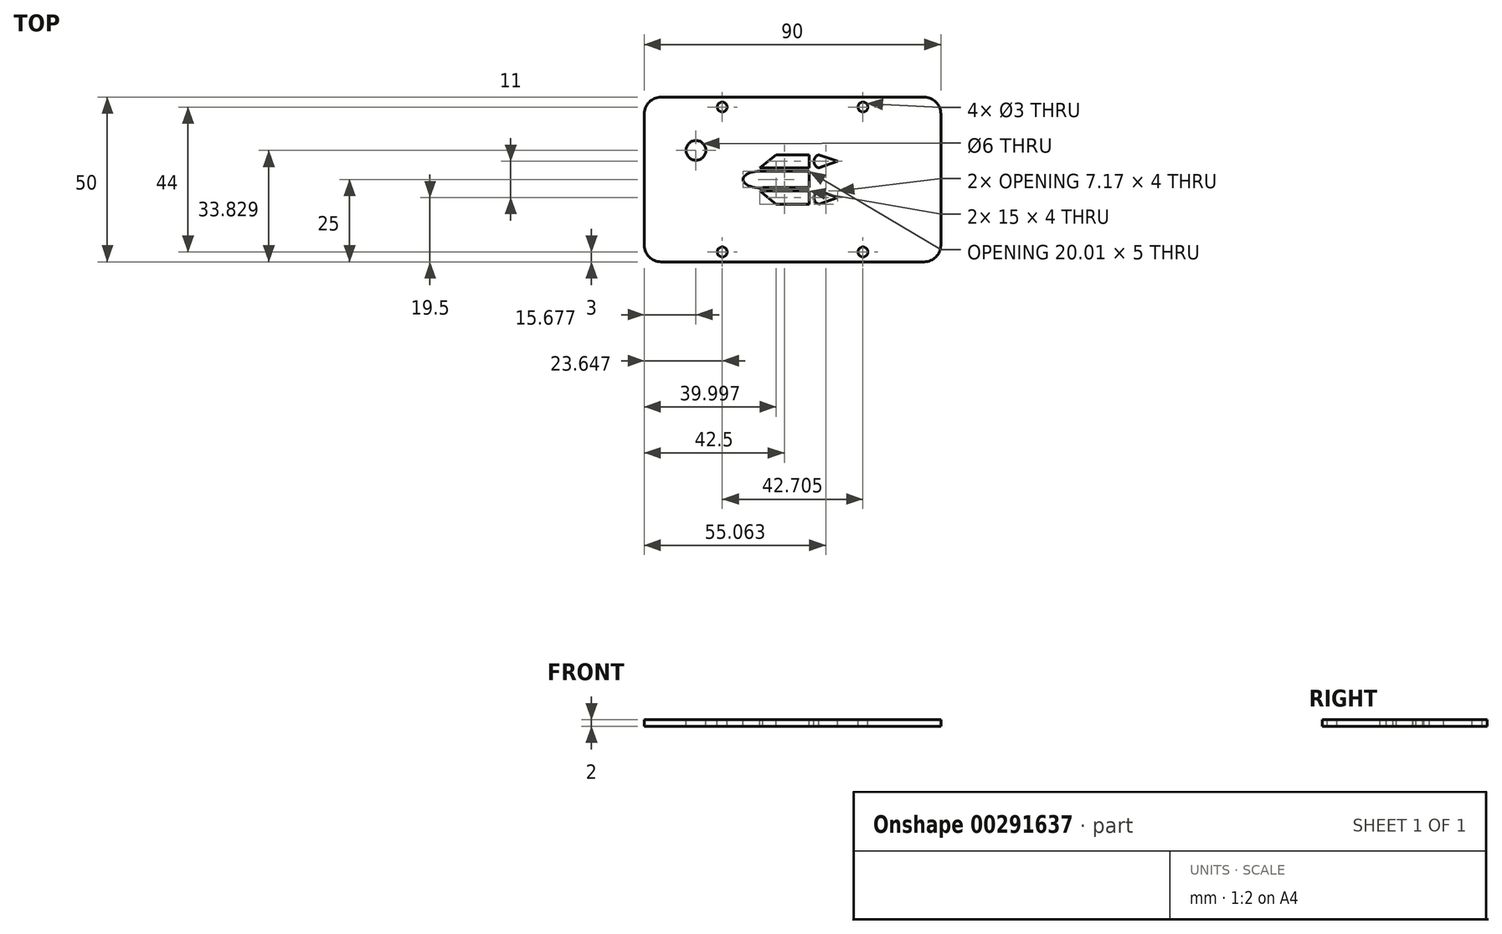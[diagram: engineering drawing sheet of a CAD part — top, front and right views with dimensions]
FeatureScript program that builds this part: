
annotation { "Feature Type Name" : "Feature", "Feature Type Description" : "" }
export const myFeature = defineFeature(function(context is Context, id is Id, definition is map)
    precondition{}
    {
        {
            var Q0;
            Q0=qCreatedBy(makeId("Top.planeOp"),FACE);
            var sketch = newSketch(context, id + "F0", { "sketchPlane" : qUnion([Q0])});
            skLineSegment(sketch, "E0.bottom", {"start": v(0, 0) * mm, "end": v(90, 0) * mm});
            skLineSegment(sketch, "E0.top", {"start": v(0, 50) * mm, "end": v(90, 50) * mm});
            skLineSegment(sketch, "E0.left", {"start": v(0, 0) * mm, "end": v(0, 50) * mm});
            skLineSegment(sketch, "E0.right", {"start": v(90, 0) * mm, "end": v(90, 50) * mm});
            skSolve(sketch);
        }
        {
            var Q0;
            Q0=qSketchRegion(id+"F0",true);
            extrude(context, id + "F1", {"entities" : qUnion([Q0]), "depth" : 2 * mm, "offsetDistance" : 25.4 * mm});
        }
        {
            var Q0;
            Q0=makeQuery(id+"F1.opExtrude","CAP_FACE",FACE,{"disambiguationData":[OSD([sQuery(id+"F0.wireOp",EDGE,"E0.bottom"),sQuery(id+"F0.wireOp",EDGE,"E0.top"),sQuery(id+"F0.wireOp",EDGE,"E0.left"),sQuery(id+"F0.wireOp",EDGE,"E0.right")])],"isStart":false});
            cPlane(context, id + "F2", {"entities" : qUnion([Q0]), "cplaneType" : CPlaneType.OFFSET, "offset" : 0 * mm, "width" : 152.4 * mm, "height" : 152.4 * mm});
        }
        {
            var Q0;
            Q0=makeQuery(id+"F1.opExtrude","SWEPT_EDGE",EDGE,{"disambiguationData":[OSD([sQuery(id+"F0.wireOp",EDGE,"E0.bottom"),sQuery(id+"F0.wireOp",EDGE,"E0.right")])]});
            fillet(context, id + "F3", {"entities" : qUnion([Q0]), "radius" : 5.08 * mm, "tangentPropagation" : true, "allowEdgeOverflow" : false});
        }
        {
            var Q0;
            Q0=makeQuery(id+"F1.opExtrude","SWEPT_EDGE",EDGE,{"disambiguationData":[OSD([sQuery(id+"F0.wireOp",EDGE,"E0.top"),sQuery(id+"F0.wireOp",EDGE,"E0.right")])]});
            fillet(context, id + "F4", {"entities" : qUnion([Q0]), "radius" : 5.08 * mm, "tangentPropagation" : true, "allowEdgeOverflow" : false});
        }
        {
            var Q0;
            Q0=makeQuery(id+"F1.opExtrude","SWEPT_EDGE",EDGE,{"disambiguationData":[OSD([sQuery(id+"F0.wireOp",EDGE,"E0.top"),sQuery(id+"F0.wireOp",EDGE,"E0.left")])]});
            fillet(context, id + "F5", {"entities" : qUnion([Q0]), "radius" : 5.08 * mm, "tangentPropagation" : true, "allowEdgeOverflow" : false});
        }
        {
            var Q0;
            Q0=makeQuery(id+"F1.opExtrude","SWEPT_EDGE",EDGE,{"disambiguationData":[OSD([sQuery(id+"F0.wireOp",EDGE,"E0.bottom"),sQuery(id+"F0.wireOp",EDGE,"E0.left")])]});
            fillet(context, id + "F6", {"entities" : qUnion([Q0]), "radius" : 5.08 * mm, "tangentPropagation" : true, "allowEdgeOverflow" : false});
        }
        {
            var Q0;
            Q0=qCreatedBy(id+"F2.planeOp",FACE);
            var sketch = newSketch(context, id + "F7", { "sketchPlane" : qUnion([Q0])});
            skLineSegment(sketch, "E1", {"start": v(45, 0) * mm, "end": v(45, 70.78) * mm});
            skLineSegment(sketch, "E2", {"start": v(0, 25) * mm, "end": v(105.16, 25) * mm});
            skSolve(sketch);
        }
        {
            var Q0;
            Q0=qCreatedBy(id+"F2.planeOp",FACE);
            var sketch = newSketch(context, id + "F8", { "sketchPlane" : qUnion([Q0])});
            skLineSegment(sketch, "E3.bottom", {"start": v(35, 27.5) * mm, "end": v(50, 27.5) * mm});
            skLineSegment(sketch, "E3.top", {"start": v(35, 22.5) * mm, "end": v(50, 22.5) * mm});
            skLineSegment(sketch, "E3.left", {"start": v(35, 27.5) * mm, "end": v(35, 22.5) * mm});
            skLineSegment(sketch, "E3.right", {"start": v(50, 27.5) * mm, "end": v(50, 22.5) * mm});
            skEllipse(sketch, "E4", {"center": v(35, 25) * mm, "majorRadius": 5 * mm, "minorRadius": 2.54 * mm, "majorAxis": v(-1, 0)});
            skLineSegment(sketch, "E5.bottom", {"start": v(40, 32.5) * mm, "end": v(50, 32.5) * mm});
            skLineSegment(sketch, "E5.top", {"start": v(40, 28.5) * mm, "end": v(50, 28.5) * mm});
            skLineSegment(sketch, "E5.left", {"start": v(40, 32.5) * mm, "end": v(40, 28.5) * mm});
            skLineSegment(sketch, "E5.right", {"start": v(50, 32.5) * mm, "end": v(50, 28.5) * mm});
            skLineSegment(sketch, "E6", {"start": v(40, 32.5) * mm, "end": v(35, 28.5) * mm});
            skLineSegment(sketch, "E7", {"start": v(35, 28.5) * mm, "end": v(40, 28.5) * mm});
            skLineSegment(sketch, "E8.MirrorCS", {"start": v(40, 17.5) * mm, "end": v(35, 21.5) * mm});
            skLineSegment(sketch, "E9.MirrorCS", {"start": v(35, 21.5) * mm, "end": v(40, 21.5) * mm});
            skLineSegment(sketch, "E10.MirrorCS", {"start": v(40, 17.5) * mm, "end": v(40, 21.5) * mm});
            skLineSegment(sketch, "E11.MirrorCS", {"start": v(40, 21.5) * mm, "end": v(50, 21.5) * mm});
            skLineSegment(sketch, "E12.MirrorCS", {"start": v(40, 17.5) * mm, "end": v(50, 17.5) * mm});
            skLineSegment(sketch, "E13.MirrorCS", {"start": v(50, 17.5) * mm, "end": v(50, 21.5) * mm});
            skArc(sketch, "E14", {"start": v(53, 32.5) * mm, "mid": v(51.48, 30.5) * mm, "end": v(53, 28.5) * mm});
            skArc(sketch, "E15.MirrorCS", {"start": v(53, 17.5) * mm, "mid": v(51.48, 19.5) * mm, "end": v(53, 21.5) * mm});
            skLineSegment(sketch, "E16", {"start": v(53, 32.5) * mm, "end": v(58.65, 30.5) * mm});
            skLineSegment(sketch, "E17", {"start": v(58.65, 30.5) * mm, "end": v(53, 28.5) * mm});
            skLineSegment(sketch, "E18.MirrorCS", {"start": v(58.65, 19.5) * mm, "end": v(53, 21.5) * mm});
            skLineSegment(sketch, "E19.MirrorCS", {"start": v(53, 17.5) * mm, "end": v(58.65, 19.5) * mm});
            skSolve(sketch);
        }
        {
            var Q0;
            Q0=qSketchRegion(id+"F8",true);
            extrude(context, id + "F9", {"entities" : qUnion([Q0]), "operationType" : NewBodyOperationType.REMOVE, "oppositeDirection" : true, "depth" : 25.4 * mm});
        }
        {
            var Q0;
            Q0=qCreatedBy(id+"F2.planeOp",FACE);
            var sketch = newSketch(context, id + "F10", { "sketchPlane" : qUnion([Q0])});
            skCircle(sketch, "E20", {"center": v(23.65, 3) * mm, "radius": 1.5 * mm});
            skCircle(sketch, "E21.MirrorC", {"center": v(66.35, 3) * mm, "radius": 1.5 * mm});
            skCircle(sketch, "E22.MirrorC", {"center": v(23.65, 47) * mm, "radius": 1.5 * mm});
            skCircle(sketch, "E23.MirrorC", {"center": v(66.35, 47) * mm, "radius": 1.5 * mm});
            skSolve(sketch);
        }
        {
            var Q0;
            Q0 = qSketchRegion(id + "F10", true);
            extrude(context, id + "F11", {"entities" : qUnion([Q0]), "operationType" : NewBodyOperationType.REMOVE, "oppositeDirection" : true, "depth" : 25.4 * mm});
        }
        {
            var Q0;
            Q0=qCreatedBy(id+"F2.planeOp",FACE);
            var sketch = newSketch(context, id + "F12", { "sketchPlane" : qUnion([Q0])});
            skCircle(sketch, "E24", {"center": v(15.68, 33.83) * mm, "radius": 3 * mm});
            skSolve(sketch);
        }
        {
            var Q0;
            Q0 = qSketchRegion(id + "F12", true);
            extrude(context, id + "F13", {"entities" : qUnion([Q0]), "operationType" : NewBodyOperationType.REMOVE, "oppositeDirection" : true, "depth" : 25.4 * mm, "offsetDistance" : 25.4 * mm});
        }
    });
